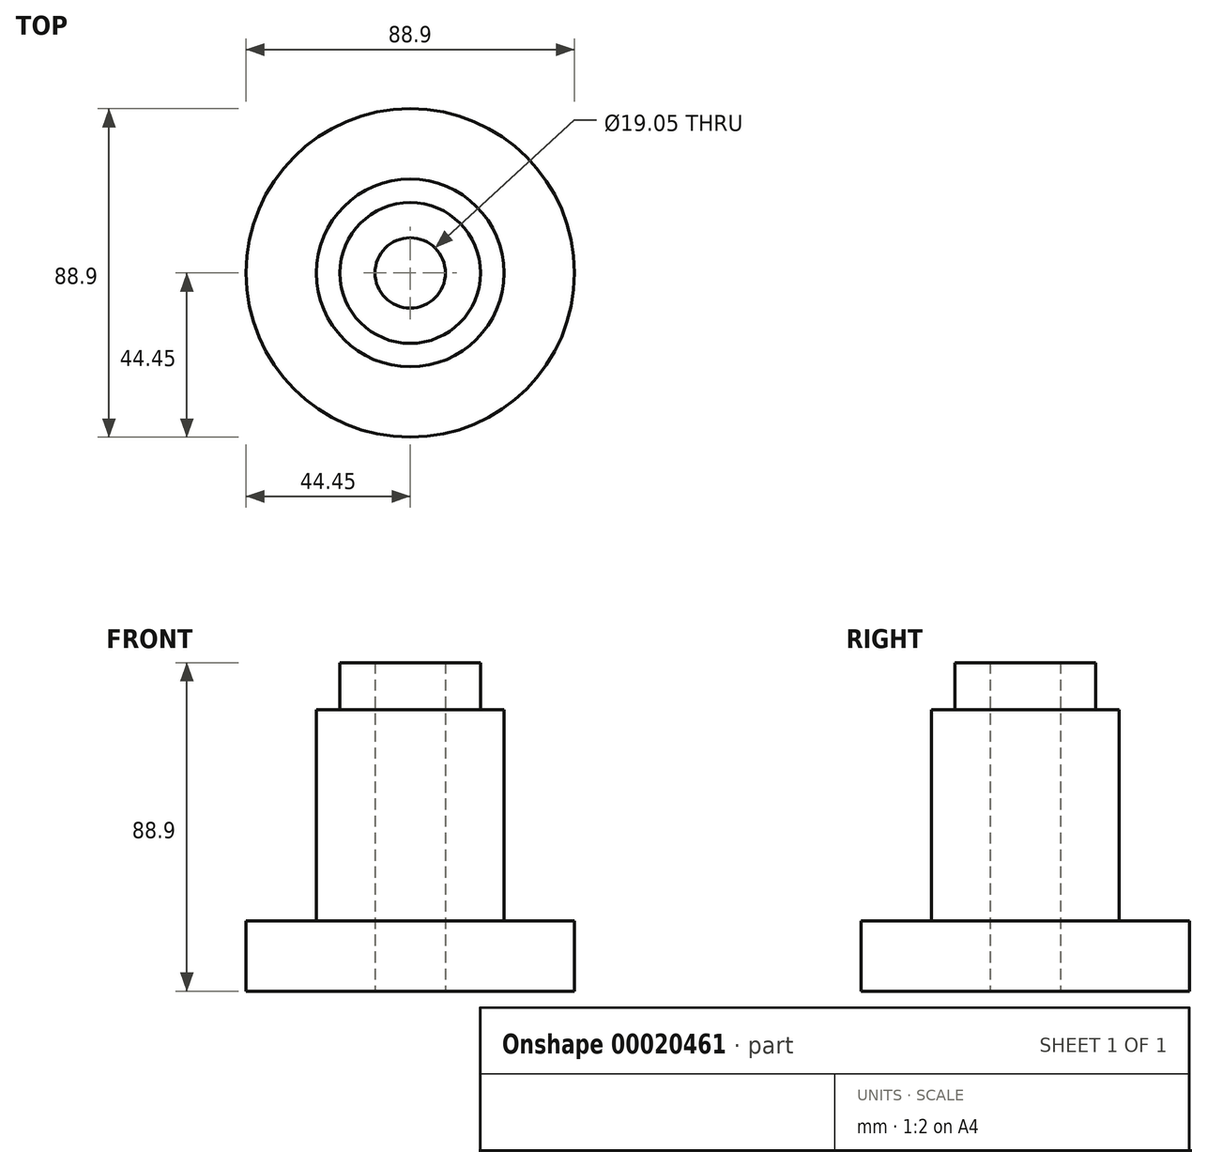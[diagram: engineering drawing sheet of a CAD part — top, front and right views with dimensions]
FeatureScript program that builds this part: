
annotation { "Feature Type Name" : "Feature", "Feature Type Description" : "" }
export const myFeature = defineFeature(function(context is Context, id is Id, definition is map)
    precondition{}
    {
        {
            var Q0;
            Q0=qCreatedBy(makeId("Top.planeOp"),FACE);
            var sketch = newSketch(context, id + "F0", { "sketchPlane" : qUnion([Q0])});
            skCircle(sketch, "E0", {"center": v(0, 0) * mm, "radius": 44.45 * mm});
            skCircle(sketch, "E1", {"center": v(0, 0) * mm, "radius": 25.4 * mm});
            skCircle(sketch, "E2", {"center": v(0, 0) * mm, "radius": 19.05 * mm});
            skCircle(sketch, "E3", {"center": v(0, 0) * mm, "radius": 9.53 * mm});
            skSolve(sketch);
        }
        {
            var Q0;
            Q0=makeQuery(id+"F0.imprint","IMPRINT",FACE,{"disambiguationData":[TD([[makeQuery(id+"F0.imprint","IMPRINT",EDGE,{"derivedFrom":sQuery(id+"F0.wireOp",EDGE,"E0")}),1.0]])]});
            extrude(context, id + "F1", {"entities" : qUnion([Q0]), "depth" : 19.05 * mm});
        }
        {
            var Q0;
            Q0=makeQuery(id+"F0.imprint","IMPRINT",FACE,{"disambiguationData":[TD([[makeQuery(id+"F0.imprint","IMPRINT",EDGE,{"derivedFrom":sQuery(id+"F0.wireOp",EDGE,"E1")}),1.0]])]});
            extrude(context, id + "F2", {"entities" : qUnion([Q0]), "operationType" : NewBodyOperationType.ADD, "depth" : 76.2 * mm});
        }
        {
            var Q0;
            Q0=makeQuery(id+"F0.imprint","IMPRINT",FACE,{"disambiguationData":[TD([[makeQuery(id+"F0.imprint","IMPRINT",EDGE,{"derivedFrom":sQuery(id+"F0.wireOp",EDGE,"E2")}),1.0]])]});
            extrude(context, id + "F3", {"entities" : qUnion([Q0]), "operationType" : NewBodyOperationType.ADD, "depth" : 88.9 * mm});
        }
    });
